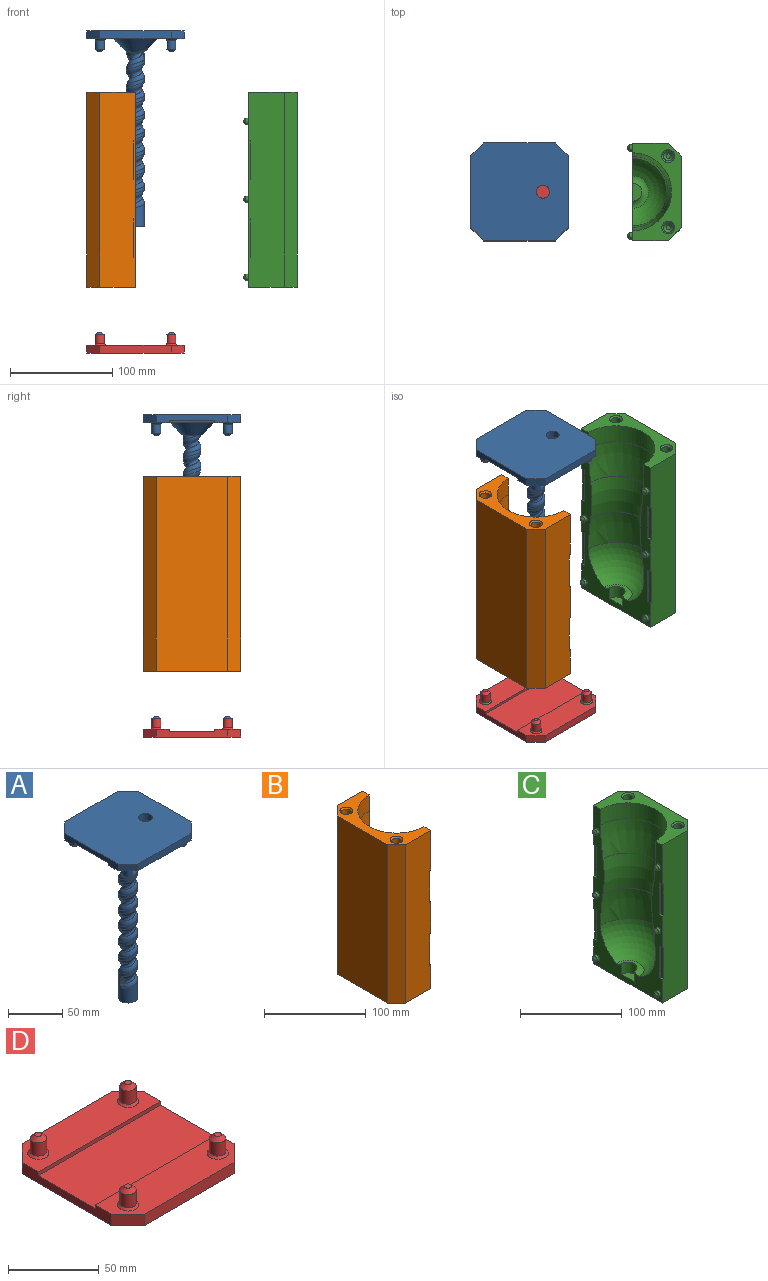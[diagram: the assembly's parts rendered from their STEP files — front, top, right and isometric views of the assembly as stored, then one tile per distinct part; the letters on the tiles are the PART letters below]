
ASSEMBLY  parts=4 mates=3
PART A: 64 faces, bbox 95.3x95.3x191.5 mm
  f0: cylinder r=8.76mm len=40.66mm, axis (0,0,1), area 1357.1mm2, adj f8,f28,f32,f33,f34,f35,f37
  f1: cylinder r=8.76mm len=17.53mm, axis (0,0,1), area 166.7mm2, adj f2,f9,f33,f43,f45
  f2: cylinder r=8.76mm len=22.31mm, axis (0,0,1), area 187mm2, adj f1,f3,f32,f33,f45
  f3: cylinder r=8.76mm len=21.01mm, axis (0,0,1), area 186.3mm2, adj f2,f4,f32,f33
  f4: cylinder r=8.76mm len=21.01mm, axis (0,0,1), area 186.3mm2, adj f3,f5,f32,f33
  f5: cylinder r=8.76mm len=21.01mm, axis (0,0,1), area 186.3mm2, adj f4,f6,f32,f33
  f6: cylinder r=8.76mm len=21.01mm, axis (0,0,1), area 186.9mm2, adj f5,f7,f32,f33
  f7: cylinder r=8.76mm len=21.01mm, axis (0,0,1), area 186.3mm2, adj f6,f8,f32,f33
  f8: cylinder r=8.76mm len=21.01mm, axis (0,0,1), area 186.3mm2, adj f0,f7,f32,f33
  f9: cone r=21.46mm half-angle=45deg, axis (0,0,1), area 1619.7mm2, adj f1,f15,f33,f40,f41,f42,f43,f63
  f10: plane 69.85x7.62mm, normal (1,0,0), area 419.4mm2, adj f14,f15,f47,f48,f49,f55,f58
  f11: plane 69.85x7.62mm, normal (0,1,0), area 532.3mm2, adj f14,f15,f55,f56
  f12: plane 69.85x7.62mm, normal (-1,0,0), area 419.4mm2, adj f14,f15,f51,f52,f53,f56,f57
  f13: plane 69.85x7.62mm, normal (0,-1,0), area 532.3mm2, adj f14,f15,f57,f58
  f14: plane 95.25x95.25mm, normal (0,0,1), area 8623.3mm2, adj f10,f11,f12,f13,f55,f56,f57,f58
  f15: plane 95.25x95.25mm, normal (0,0,-1), area 5321.7mm2, adj f9,f10,f11,f12,f13,f47,f49,f50
  f16: cylinder r=4.57mm len=9.14mm, axis (0,0,1), area 255.4mm2, adj f26,f60
  f17: plane 4.06x4.06mm, normal (0,0,-1), area 13mm2, adj f26
  f18: cylinder r=4.57mm len=9.14mm, axis (0,0,1), area 255.4mm2, adj f27,f62
  f19: plane 4.06x4.06mm, normal (0,0,-1), area 13mm2, adj f27
  f20: cylinder r=4.57mm len=9.14mm, axis (0,0,1), area 255.4mm2, adj f25,f61
  f21: plane 4.06x4.06mm, normal (0,0,-1), area 13mm2, adj f25
  f22: cylinder r=4.57mm len=9.14mm, axis (0,0,1), area 255.4mm2, adj f24,f59
  f23: plane 4.06x4.06mm, normal (0,0,-1), area 13mm2, adj f24
  f24: cone r=2.03mm half-angle=45deg, axis (0,0,1), area 74.5mm2, adj f22,f23
  f25: cone r=2.03mm half-angle=45deg, axis (0,0,1), area 74.5mm2, adj f20,f21
  f26: cone r=2.03mm half-angle=45deg, axis (0,0,1), area 74.5mm2, adj f16,f17
  f27: cone r=2.03mm half-angle=45deg, axis (0,0,1), area 74.5mm2, adj f18,f19
  f28: plane 17.53x17.53mm, normal (0,0,-1), area 241.2mm2, adj f0
  f29: plane 2.69x0.65mm, normal (0,-1,0), area 1.2mm2, adj f35,f36,f38,f39
  f30: plane 3.18x1.49mm, normal (0,-1,0), area 1.4mm2, adj f41,f43,f44,f46
  f31: bspline ~162.56x25.1mm, area 1719.4mm2, adj f32,f33,f38,f40,f44
  f32: bspline ~154.2x17.94mm, area 2322.7mm2, adj f0,f2,f3,f4,f5,f6,f7,f8
  f33: bspline ~149.21x17.94mm, area 2248.8mm2, adj f0,f1,f2,f3,f4,f5,f6,f7
  f34: bspline ~6.52x2.59mm, area 4.3mm2, adj f0,f35,f36
  f35: cylinder r=1.27mm len=2.69mm, axis (0,0,1), area 6mm2, adj f0,f29,f34,f37
  f36: bspline ~7.18x3.82mm, area 3.5mm2, adj f29,f33,f34,f38
  f37: bspline ~6.59x2.59mm, area 4.6mm2, adj f0,f35,f39
  f38: bspline ~5.63x2.28mm, area 7.5mm2, adj f29,f31,f36,f39
  f39: bspline ~7.39x4.41mm, area 5.5mm2, adj f29,f32,f37,f38
  f40: bspline ~11.85x7.2mm, area 15.7mm2, adj f9,f31,f33,f42
  f41: bspline ~3.2x3.19mm, area 2mm2, adj f9,f30,f42,f43
  f42: bspline ~4.17x3.39mm, area 7.2mm2, adj f9,f40,f41,f44
  f43: cylinder r=1.27mm len=2.35mm, axis (0,0,1), area 4.4mm2, adj f1,f9,f30,f41,f45
  f44: bspline ~6.17x4.96mm, area 14.8mm2, adj f30,f31,f42,f46
  f45: bspline ~6.52x2.59mm, area 4.9mm2, adj f1,f2,f43,f46
  f46: bspline ~6.86x3.47mm, area 3.5mm2, adj f30,f32,f44,f45
  f47: plane 16.51x2.54mm, normal (0,-1,0), area 41.9mm2, adj f10,f15,f48,f50
  f48: plane 44.45x16.51mm, normal (0,0,-1), area 733.9mm2, adj f10,f47,f49,f50
  f49: plane 16.51x2.54mm, normal (0,1,0), area 41.9mm2, adj f10,f15,f48,f50
  f50: plane 44.45x2.54mm, normal (1,0,0), area 112.9mm2, adj f15,f47,f48,f49
  f51: plane 16.51x2.54mm, normal (0,1,0), area 41.9mm2, adj f12,f15,f52,f54
  f52: plane 44.45x16.51mm, normal (0,0,-1), area 733.9mm2, adj f12,f51,f53,f54
  f53: plane 16.51x2.54mm, normal (0,-1,0), area 41.9mm2, adj f12,f15,f52,f54
  f54: plane 44.45x2.54mm, normal (-1,0,0), area 112.9mm2, adj f15,f51,f52,f53
  f55: plane 12.7x12.7mm, normal (0.71,0.71,0), area 136.9mm2, adj f10,f11,f14,f15
  f56: plane 12.7x12.7mm, normal (-0.71,0.71,0), area 136.9mm2, adj f11,f12,f14,f15
  f57: plane 12.7x12.7mm, normal (-0.71,-0.71,0), area 136.9mm2, adj f12,f13,f14,f15
  f58: plane 12.7x12.7mm, normal (0.71,-0.71,0), area 136.9mm2, adj f10,f13,f14,f15
  f59: cone r=4.57mm half-angle=45deg, axis (0,0,1), area 58.8mm2, adj f15,f22
  f60: cone r=4.57mm half-angle=45deg, axis (0,0,1), area 58.8mm2, adj f15,f16
  f61: cone r=4.57mm half-angle=45deg, axis (0,0,1), area 58.8mm2, adj f15,f20
  f62: cone r=4.57mm half-angle=45deg, axis (0,0,1), area 58.8mm2, adj f15,f18
  f63: cylinder r=6.35mm len=12.7mm, axis (0,0,1), area 336.1mm2, adj f9,f14,f15
PART B: 66 faces, bbox 75.6x151.2x201.3 mm
  f0: plane 190.5x95.25mm, normal (1,0,0), area 4910.7mm2, adj f1,f9,f10,f11,f12,f13,f14,f15
  f1: plane 190.5x34.93mm, normal (0,-1,0), area 6532.2mm2, adj f0,f17,f18,f52,f53,f54,f56,f57
  f2: plane 4.45x4.45mm, normal (0,0,1), area 15.5mm2, adj f4
  f3: plane 4.45x4.45mm, normal (0,0,1), area 15.5mm2, adj f5
  f4: cone r=2.22mm half-angle=45deg, axis (0,0,1), area 78.8mm2, adj f2,f6
  f5: cone r=2.22mm half-angle=45deg, axis (0,0,1), area 78.8mm2, adj f3,f7
  f6: cylinder r=4.76mm len=9.53mm, axis (0,0,1), area 258.4mm2, adj f4,f65
  f7: cylinder r=4.76mm len=9.53mm, axis (0,0,1), area 258.4mm2, adj f5,f64
  f8: plane 190.5x69.85mm, normal (-1,0,0), area 13306.4mm2, adj f17,f18,f60,f61
  f9: cylinder r=38.1mm len=76.2mm, axis (0,0,1), area 2280.2mm2, adj f0,f16,f17
  f10: torus R=160.02mm, axis (0,0,1), area 4507.3mm2, adj f0,f11,f16
  f11: revolved ~76.2x39.09mm, area 4565mm2, adj f0,f10,f12
  f12: sphere r=38.1mm, area 4145.6mm2, adj f0,f11,f13
  f13: torus R=14.91mm, axis (0,0,1), area 301.3mm2, adj f0,f12,f14
  f14: cylinder r=8.89mm len=17.78mm, axis (0,0,1), area 354.7mm2, adj f0,f13,f15
  f15: plane 17.78x8.89mm, normal (0,0,1), area 124.1mm2, adj f0,f14
  f16: revolved ~76.2x39.09mm, area 4565mm2, adj f0,f9,f10
  f17: plane 95.25x47.63mm, normal (0,0,1), area 1846.5mm2, adj f0,f1,f8,f9,f19,f60,f61,f64
  f18: plane 95.25x47.63mm, normal (0,0,-1), area 4126.7mm2, adj f0,f1,f8,f19,f60,f61,f62,f63
  f19: plane 190.5x34.93mm, normal (0,1,0), area 6532.2mm2, adj f0,f17,f18,f44,f45,f46,f48,f49
  f20: cylinder r=3.17mm len=6.35mm, axis (1,0,0), area 68.4mm2, adj f0,f37
  f21: plane 2.54x2.54mm, normal (1,0,0), area 5.1mm2, adj f37
  f22: cylinder r=3.17mm len=6.35mm, axis (1,0,0), area 68.4mm2, adj f0,f36
  f23: plane 2.54x2.54mm, normal (1,0,0), area 5.1mm2, adj f36
  f24: cylinder r=3.17mm len=6.35mm, axis (1,0,0), area 68.4mm2, adj f0,f35
  f25: plane 2.54x2.54mm, normal (1,0,0), area 5.1mm2, adj f35
  f26: cylinder r=3.17mm len=6.35mm, axis (1,0,0), area 68.4mm2, adj f0,f34
  f27: plane 2.54x2.54mm, normal (1,0,0), area 5.1mm2, adj f34
  f28: cylinder r=3.17mm len=6.35mm, axis (1,0,0), area 68.4mm2, adj f0,f33
  f29: plane 2.54x2.54mm, normal (1,0,0), area 5.1mm2, adj f33
  f30: cylinder r=3.17mm len=6.35mm, axis (1,0,0), area 68.4mm2, adj f0,f32
  f31: plane 2.54x2.54mm, normal (1,0,0), area 5.1mm2, adj f32
  f32: cone r=3.17mm half-angle=45deg, axis (1,0,0), area 37.6mm2, adj f30,f31
  f33: cone r=3.17mm half-angle=45deg, axis (1,0,0), area 37.6mm2, adj f28,f29
  f34: cone r=3.17mm half-angle=45deg, axis (1,0,0), area 37.6mm2, adj f26,f27
  f35: cone r=1.27mm half-angle=45deg, axis (1,0,0), area 37.6mm2, adj f24,f25
  f36: cone r=1.27mm half-angle=45deg, axis (1,0,0), area 37.6mm2, adj f22,f23
  f37: cone r=1.27mm half-angle=45deg, axis (1,0,0), area 37.6mm2, adj f20,f21
  f38: cylinder r=4.76mm len=9.53mm, axis (0,0,-1), area 258.4mm2, adj f42,f63
  f39: plane 4.45x4.45mm, normal (0,0,-1), area 15.5mm2, adj f42
  f40: cylinder r=4.76mm len=9.53mm, axis (0,0,-1), area 258.4mm2, adj f43,f62
  f41: plane 4.45x4.45mm, normal (0,0,-1), area 15.5mm2, adj f43
  f42: cone r=4.76mm half-angle=45deg, axis (0,0,-1), area 78.8mm2, adj f38,f39
  f43: cone r=4.76mm half-angle=45deg, axis (0,0,-1), area 78.8mm2, adj f40,f41
  f44: plane 3.81x1.59mm, normal (0,0,1), area 6mm2, adj f0,f19,f45,f47
  f45: plane 38.1x3.81mm, normal (1,0,0), area 145.2mm2, adj f19,f44,f46,f47
  f46: plane 3.81x1.59mm, normal (0,0,-1), area 6mm2, adj f0,f19,f45,f47
  f47: plane 38.1x1.59mm, normal (0,1,0), area 60.5mm2, adj f0,f44,f45,f46
  f48: plane 3.81x1.59mm, normal (0,0,1), area 6mm2, adj f0,f19,f49,f51
  f49: plane 38.1x3.81mm, normal (1,0,0), area 145.2mm2, adj f19,f48,f50,f51
  f50: plane 3.81x1.59mm, normal (0,0,-1), area 6mm2, adj f0,f19,f49,f51
  f51: plane 38.1x1.59mm, normal (0,1,0), area 60.5mm2, adj f0,f48,f49,f50
  f52: plane 3.81x1.59mm, normal (0,0,1), area 6mm2, adj f0,f1,f54,f55
  f53: plane 3.81x1.59mm, normal (0,0,-1), area 6mm2, adj f0,f1,f54,f55
  f54: plane 38.1x3.81mm, normal (1,0,0), area 145.2mm2, adj f1,f52,f53,f55
  f55: plane 38.1x1.59mm, normal (0,-1,0), area 60.5mm2, adj f0,f52,f53,f54
  f56: plane 3.81x1.59mm, normal (0,0,-1), area 6mm2, adj f0,f1,f57,f59
  f57: plane 38.1x3.81mm, normal (1,0,0), area 145.2mm2, adj f1,f56,f58,f59
  f58: plane 3.81x1.59mm, normal (0,0,1), area 6mm2, adj f0,f1,f57,f59
  f59: plane 38.1x1.59mm, normal (0,-1,0), area 60.5mm2, adj f0,f56,f57,f58
  f60: plane 190.5x12.7mm, normal (-0.71,0.71,0), area 3421.5mm2, adj f8,f17,f18,f19
  f61: plane 190.5x12.7mm, normal (-0.71,-0.71,0), area 3421.5mm2, adj f1,f8,f17,f18
  f62: cone r=6.29mm half-angle=45deg, axis (0,0,-1), area 74.8mm2, adj f18,f40
  f63: cone r=6.29mm half-angle=45deg, axis (0,0,-1), area 74.8mm2, adj f18,f38
  f64: cone r=4.76mm half-angle=45deg, axis (0,0,1), area 74.8mm2, adj f7,f17
  f65: cone r=4.76mm half-angle=45deg, axis (0,0,1), area 74.8mm2, adj f6,f17
PART C: 66 faces, bbox 80.7x151.2x201.3 mm
  f0: plane 190.5x95.25mm, normal (-1,0,0), area 4925.6mm2, adj f1,f3,f4,f5,f6,f7,f8,f9
  f1: plane 190.5x34.93mm, normal (0,-1,0), area 6532.2mm2, adj f0,f4,f5,f52,f53,f55,f56,f57
  f2: plane 190.5x69.85mm, normal (1,0,0), area 13306.4mm2, adj f4,f5,f60,f61
  f3: plane 190.5x34.93mm, normal (0,1,0), area 6532.2mm2, adj f0,f4,f5,f44,f45,f47,f48,f49
  f4: plane 95.25x47.63mm, normal (0,0,1), area 1846.5mm2, adj f0,f1,f2,f3,f7,f60,f61,f64
  f5: plane 95.25x47.63mm, normal (0,0,-1), area 4126.7mm2, adj f0,f1,f2,f3,f60,f61,f62,f63
  f6: revolved ~76.2x39.09mm, area 4565mm2, adj f0,f7,f13
  f7: cylinder r=38.1mm len=76.2mm, axis (0,0,1), area 2280.2mm2, adj f0,f4,f6
  f8: plane 17.78x8.89mm, normal (0,0,1), area 124.1mm2, adj f0,f9
  f9: cylinder r=8.89mm len=17.78mm, axis (0,0,1), area 354.7mm2, adj f0,f8,f10
  f10: torus R=14.91mm, axis (0,0,1), area 301.3mm2, adj f0,f9,f11
  f11: sphere r=38.1mm, area 4145.6mm2, adj f0,f10,f12
  f12: revolved ~76.2x39.09mm, area 4565mm2, adj f0,f11,f13
  f13: torus R=160.02mm, axis (0,0,1), area 4507.3mm2, adj f0,f6,f12
  f14: cylinder r=4.76mm len=9.53mm, axis (0,0,1), area 258.4mm2, adj f18,f65
  f15: plane 4.45x4.45mm, normal (0,0,1), area 15.5mm2, adj f18
  f16: cylinder r=4.76mm len=9.53mm, axis (0,0,1), area 258.4mm2, adj f19,f64
  f17: plane 4.45x4.45mm, normal (0,0,1), area 15.5mm2, adj f19
  f18: cone r=2.22mm half-angle=45deg, axis (0,0,1), area 78.8mm2, adj f14,f15
  f19: cone r=2.22mm half-angle=45deg, axis (0,0,1), area 78.8mm2, adj f16,f17
  f20: cylinder r=3.05mm len=6.1mm, axis (1,0,0), area 60.8mm2, adj f0,f35
  f21: plane 2.29x2.29mm, normal (-1,0,0), area 4.1mm2, adj f35
  f22: cylinder r=3.05mm len=6.1mm, axis (1,0,0), area 60.8mm2, adj f0,f36
  f23: plane 2.29x2.29mm, normal (-1,0,0), area 4.1mm2, adj f36
  f24: cylinder r=3.05mm len=6.1mm, axis (1,0,0), area 60.8mm2, adj f0,f37
  f25: plane 2.29x2.29mm, normal (-1,0,0), area 4.1mm2, adj f37
  f26: cylinder r=3.05mm len=6.1mm, axis (1,0,0), area 60.8mm2, adj f0,f33
  f27: plane 2.29x2.29mm, normal (-1,0,0), area 4.1mm2, adj f33
  f28: cylinder r=3.05mm len=6.1mm, axis (1,0,0), area 60.8mm2, adj f0,f32
  f29: plane 2.29x2.29mm, normal (-1,0,0), area 4.1mm2, adj f32
  f30: cylinder r=3.05mm len=6.1mm, axis (1,0,0), area 60.8mm2, adj f0,f34
  f31: plane 2.29x2.29mm, normal (-1,0,0), area 4.1mm2, adj f34
  f32: cone r=1.14mm half-angle=45deg, axis (1,0,0), area 35.5mm2, adj f28,f29
  f33: cone r=1.14mm half-angle=45deg, axis (1,0,0), area 35.5mm2, adj f26,f27
  f34: cone r=1.14mm half-angle=45deg, axis (1,0,0), area 35.5mm2, adj f30,f31
  f35: cone r=3.05mm half-angle=45deg, axis (1,0,0), area 35.5mm2, adj f20,f21
  f36: cone r=3.05mm half-angle=45deg, axis (1,0,0), area 35.5mm2, adj f22,f23
  f37: cone r=3.05mm half-angle=45deg, axis (1,0,0), area 35.5mm2, adj f24,f25
  f38: cylinder r=4.76mm len=9.53mm, axis (0,0,-1), area 258.4mm2, adj f42,f63
  f39: plane 4.45x4.45mm, normal (0,0,-1), area 15.5mm2, adj f42
  f40: cylinder r=4.76mm len=9.53mm, axis (0,0,-1), area 258.4mm2, adj f43,f62
  f41: plane 4.45x4.45mm, normal (0,0,-1), area 15.5mm2, adj f43
  f42: cone r=4.76mm half-angle=45deg, axis (0,0,-1), area 78.8mm2, adj f38,f39
  f43: cone r=4.76mm half-angle=45deg, axis (0,0,-1), area 78.8mm2, adj f40,f41
  f44: plane 3.81x1.59mm, normal (0,0,1), area 6mm2, adj f0,f3,f46,f47
  f45: plane 3.81x1.59mm, normal (0,0,-1), area 6mm2, adj f0,f3,f46,f47
  f46: plane 38.1x1.59mm, normal (0,1,0), area 60.5mm2, adj f0,f44,f45,f47
  f47: plane 38.1x3.81mm, normal (-1,0,0), area 145.2mm2, adj f3,f44,f45,f46
  f48: plane 3.81x1.59mm, normal (0,0,1), area 6mm2, adj f0,f3,f50,f51
  f49: plane 3.81x1.59mm, normal (0,0,-1), area 6mm2, adj f0,f3,f50,f51
  f50: plane 38.1x1.59mm, normal (0,1,0), area 60.5mm2, adj f0,f48,f49,f51
  f51: plane 38.1x3.81mm, normal (-1,0,0), area 145.2mm2, adj f3,f48,f49,f50
  f52: plane 3.81x1.59mm, normal (0,0,1), area 6mm2, adj f0,f1,f54,f55
  f53: plane 3.81x1.59mm, normal (0,0,-1), area 6mm2, adj f0,f1,f54,f55
  f54: plane 38.1x1.59mm, normal (0,-1,0), area 60.5mm2, adj f0,f52,f53,f55
  f55: plane 38.1x3.81mm, normal (-1,0,0), area 145.2mm2, adj f1,f52,f53,f54
  f56: plane 3.81x1.59mm, normal (0,0,-1), area 6mm2, adj f0,f1,f58,f59
  f57: plane 3.81x1.59mm, normal (0,0,1), area 6mm2, adj f0,f1,f58,f59
  f58: plane 38.1x1.59mm, normal (0,-1,0), area 60.5mm2, adj f0,f56,f57,f59
  f59: plane 38.1x3.81mm, normal (-1,0,0), area 145.2mm2, adj f1,f56,f57,f58
  f60: plane 190.5x12.7mm, normal (0.71,0.71,0), area 3421.5mm2, adj f2,f3,f4,f5
  f61: plane 190.5x12.7mm, normal (0.71,-0.71,0), area 3421.5mm2, adj f1,f2,f4,f5
  f62: cone r=6.29mm half-angle=45deg, axis (0,0,-1), area 74.8mm2, adj f5,f40
  f63: cone r=6.29mm half-angle=45deg, axis (0,0,-1), area 74.8mm2, adj f5,f38
  f64: cone r=4.76mm half-angle=45deg, axis (0,0,1), area 74.8mm2, adj f4,f16
  f65: cone r=4.76mm half-angle=45deg, axis (0,0,1), area 74.8mm2, adj f4,f14
PART D: 30 faces, bbox 95.3x95.3x20.3 mm
  f0: plane 95.25x25.4mm, normal (0,0,1), area 2043.6mm2, adj f1,f2,f3,f19,f22,f23,f26,f29
  f1: plane 69.85x7.62mm, normal (-1,0,0), area 419.4mm2, adj f0,f5,f6,f19,f20,f21,f23,f24
  f2: plane 69.85x7.62mm, normal (1,0,0), area 419.4mm2, adj f0,f5,f6,f19,f20,f21,f22,f25
  f3: plane 69.85x7.62mm, normal (0,1,0), area 532.3mm2, adj f0,f5,f22,f23
  f4: plane 69.85x7.62mm, normal (0,-1,0), area 532.3mm2, adj f5,f6,f24,f25
  f5: plane 95.25x95.25mm, normal (0,0,-1), area 8750mm2, adj f1,f2,f3,f4,f22,f23,f24,f25
  f6: plane 95.25x25.4mm, normal (0,0,1), area 2043.6mm2, adj f1,f2,f4,f20,f24,f25,f27,f28
  f7: cylinder r=4.57mm len=9.14mm, axis (0,0,-1), area 255.4mm2, adj f16,f27
  f8: plane 4.06x4.06mm, normal (0,0,1), area 13mm2, adj f16
  f9: cylinder r=4.57mm len=9.14mm, axis (0,0,-1), area 255.4mm2, adj f15,f28
  f10: plane 4.06x4.06mm, normal (0,0,1), area 13mm2, adj f15
  f11: cylinder r=4.57mm len=9.14mm, axis (0,0,-1), area 255.4mm2, adj f17,f29
  f12: plane 4.06x4.06mm, normal (0,0,1), area 13mm2, adj f17
  f13: cylinder r=4.57mm len=9.14mm, axis (0,0,-1), area 255.4mm2, adj f18,f26
  f14: plane 4.06x4.06mm, normal (0,0,1), area 13mm2, adj f18
  f15: cone r=2.03mm half-angle=45deg, axis (0,0,-1), area 74.5mm2, adj f9,f10
  f16: cone r=2.03mm half-angle=45deg, axis (0,0,-1), area 74.5mm2, adj f7,f8
  f17: cone r=2.03mm half-angle=45deg, axis (0,0,-1), area 74.5mm2, adj f11,f12
  f18: cone r=2.03mm half-angle=45deg, axis (0,0,-1), area 74.5mm2, adj f13,f14
  f19: plane 95.25x2.54mm, normal (0,-1,0), area 241.9mm2, adj f0,f1,f2,f21
  f20: plane 95.25x2.54mm, normal (0,1,0), area 241.9mm2, adj f1,f2,f6,f21
  f21: plane 95.25x44.45mm, normal (0,0,1), area 4233.9mm2, adj f1,f2,f19,f20
  f22: plane 12.7x12.7mm, normal (0.71,0.71,0), area 136.9mm2, adj f0,f2,f3,f5
  f23: plane 12.7x12.7mm, normal (-0.71,0.71,0), area 136.9mm2, adj f0,f1,f3,f5
  f24: plane 12.7x12.7mm, normal (-0.71,-0.71,0), area 136.9mm2, adj f1,f4,f5,f6
  f25: plane 12.7x12.7mm, normal (0.71,-0.71,0), area 136.9mm2, adj f2,f4,f5,f6
  f26: cone r=4.57mm half-angle=45deg, axis (0,0,-1), area 58.8mm2, adj f0,f13
  f27: cone r=4.57mm half-angle=45deg, axis (0,0,-1), area 58.8mm2, adj f6,f7
  f28: cone r=4.57mm half-angle=45deg, axis (0,0,-1), area 58.8mm2, adj f6,f9
  f29: cone r=4.57mm half-angle=45deg, axis (0,0,-1), area 58.8mm2, adj f0,f11
PLACE A t=(0,0,84.96)mm
PLACE B t=(0,0,32.67)mm
PLACE C t=(110.54,0,32.67)mm
PLACE D t=(0,0,-24.13)mm
MATE slider A.f18 <-> B.f5  axis (0,0,1) through (-34.93,-34.92,274.19)mm
MATE slider B.f20 <-> C.f24  axis (1,0,0) through (0,-42.86,194.6)mm
MATE slider B.f5 <-> D.f7  axis (0,0,-1) through (-34.93,-34.92,32.67)mm
